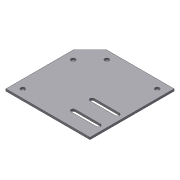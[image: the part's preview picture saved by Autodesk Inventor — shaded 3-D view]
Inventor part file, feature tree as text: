
AUTODESK INVENTOR PART (.ipt)
format: ipt  version: 2012 (Build 160160000, 160)  size: 101,888 bytes
history: native  units: in
note: dims shown in document units (in); Inventor stores cm internally (conversion verified against a paired STEP export)
features: extrude x1, chamfer x1, sketch x1
ambient origin geometry x8: Origin, YZ Plane, XZ Plane, XY Plane, X Axis, Y Axis, Z Axis, Center Point
feature tree (3):
  extrude  "Extrusion3"  Depth=1.5in
  chamfer  "Chamfer1"  Distance=3.125in
  sketch  "Sketch2"  dims[d7=5.0in d18=1.5in d19=3.125in d22=0.5in d23=3.0in d24=3.0in d25=0.25in d26=0.125in d27=0.0in d28=0.5in d29=0.5in d30=1.5in d31=5.0in d32=0.375in d33=1.0in d34=0.125in d35=45.0deg d36=0.5in d39=0.875in d40=1.125in d41=3.0in]
